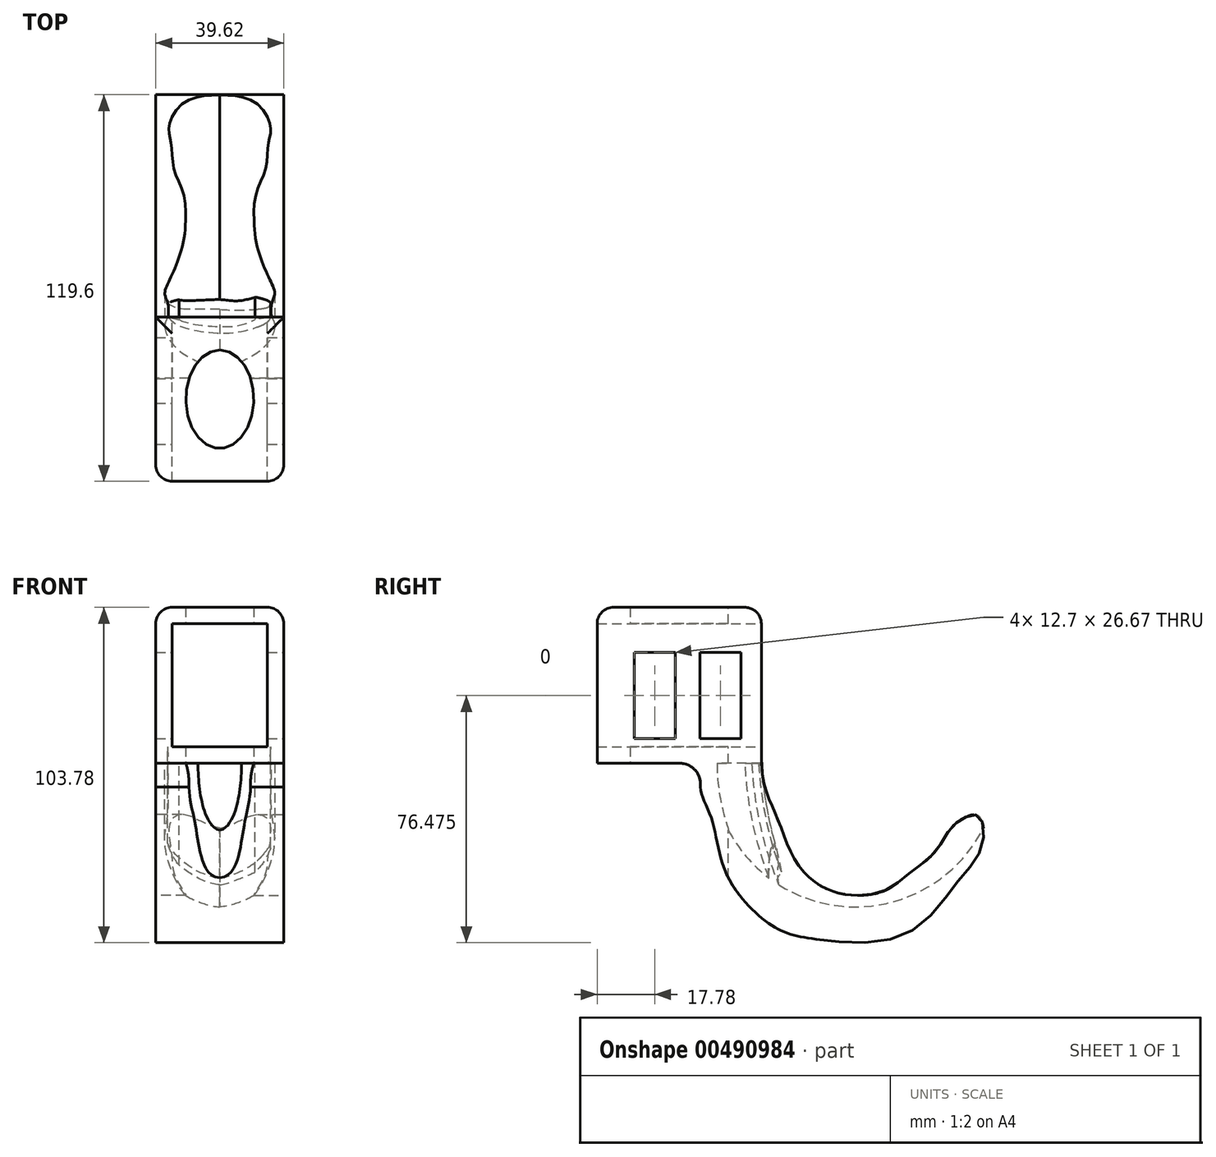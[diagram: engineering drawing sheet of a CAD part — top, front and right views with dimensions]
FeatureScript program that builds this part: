
annotation { "Feature Type Name" : "Feature", "Feature Type Description" : "" }
export const myFeature = defineFeature(function(context is Context, id is Id, definition is map)
    precondition{}
    {
        {
            var Q0;
            Q0=qCreatedBy(makeId("Front.planeOp"),FACE);
            var sketch = newSketch(context, id + "F0", { "sketchPlane" : qUnion([Q0])});
            skLineSegment(sketch, "E0", {"start": v(0, 0) * mm, "end": v(19.81, 0) * mm});
            skLineSegment(sketch, "E1", {"start": v(19.81, 0) * mm, "end": v(19.81, 48.26) * mm});
            skLineSegment(sketch, "E2", {"start": v(19.81, 48.26) * mm, "end": v(0, 48.26) * mm});
            skLineSegment(sketch, "E3.MirrorCS", {"start": v(0, 0) * mm, "end": v(-19.81, 0) * mm});
            skLineSegment(sketch, "E4.MirrorCS", {"start": v(-19.81, 0) * mm, "end": v(-19.81, 48.26) * mm});
            skLineSegment(sketch, "E5.MirrorCS", {"start": v(-19.81, 48.26) * mm, "end": v(0, 48.26) * mm});
            skLineSegment(sketch, "E6.0", {"start": v(-14.73, 5.08) * mm, "end": v(-14.73, 43.18) * mm});
            skLineSegment(sketch, "E6.1", {"start": v(14.73, 43.18) * mm, "end": v(0, 43.18) * mm});
            skLineSegment(sketch, "E6.2", {"start": v(14.73, 5.08) * mm, "end": v(14.73, 43.18) * mm});
            skLineSegment(sketch, "E6.3", {"start": v(-14.73, 43.18) * mm, "end": v(0, 43.18) * mm});
            skLineSegment(sketch, "E6.4", {"start": v(0, 5.08) * mm, "end": v(14.73, 5.08) * mm});
            skLineSegment(sketch, "E6.5", {"start": v(0, 5.08) * mm, "end": v(-14.73, 5.08) * mm});
            skSolve(sketch);
        }
        {
            var Q0;
            Q0 = qSketchRegion(id + "F0", true);
            extrude(context, id + "F1", {"entities" : qUnion([Q0]), "depth" : 50.8 * mm});
        }
        {
            var Q0;
            Q0=qCreatedBy(makeId("Right.planeOp"),FACE);
            var sketch = newSketch(context, id + "F2", { "sketchPlane" : qUnion([Q0])});
            skLineSegment(sketch, "E7.0", {"start": v(-50.8, 0) * mm, "end": v(-25.2, 0) * mm});
            skLineSegment(sketch, "E8", {"start": v(0, 0) * mm, "end": v(0, -1.58) * mm});
            skLineSegment(sketch, "E9", {"start": v(0, -1.58) * mm, "end": v(0, -40.64) * mm, "construction": true});
            skFitSpline(sketch, "E10", {"points": [v(0, 0) * mm, v(4.67, -16.3) * mm, v(11.2, -31.15) * mm, v(20.7, -39.07) * mm, v(29.8, -40.85) * mm, v(38.91, -39.07) * mm, v(46.44, -33.53) * mm, v(53.56, -27.6) * mm, v(58.7, -20.07) * mm, v(63.67, -16.45) * mm, v(67.42, -16.45) * mm, v(68.21, -25.8) * mm, v(60.67, -36.73) * mm, v(44.36, -53) * mm, v(16.9, -54.44) * mm, v(3.5, -50.33) * mm, v(-10.79, -34.25) * mm, v(-15.43, -17.04) * mm, v(-18.85, -7.4) * mm], "startDerivative": vector(15.82, -363.71) * mm, "endDerivative": vector(3.67, 160.8) * mm});
            skLineSegment(sketch, "E11", {"start": v(-18.85, -7.4) * mm, "end": v(-18.85, -6.35) * mm});
            skPoint(sketch, "E12.newPointA", {"position": v(-18.85, 0) * mm});
            skArc(sketch, "E12.filletArc", {"start": v(-18.85, -6.35) * mm, "mid": v(-20.71, -1.86) * mm, "end": v(-25.2, 0) * mm});
            skLineSegment(sketch, "E13", {"start": v(-25.2, 0) * mm, "end": v(0, 0) * mm});
            skLineSegment(sketch, "E14", {"start": v(16.9, -54.44) * mm, "end": v(-63.55, -54.44) * mm});
            skLineSegment(sketch, "E15", {"start": v(29.8, -40.85) * mm, "end": v(-33.2, -40.85) * mm});
            skSolve(sketch);
        }
        {
            var Q0;
            Q0 = qSketchRegion(id + "F2", true);
            var Q1;
            Q1=makeQuery(id+"F1.opExtrude","SWEPT_FACE",FACE,{"disambiguationData":[OSD([sQuery(id+"F0.wireOp",EDGE,"E1")])]});
            var Q2;
            Q2=makeQuery(id+"F1.opExtrude","SWEPT_FACE",FACE,{"disambiguationData":[OSD([sQuery(id+"F0.wireOp",EDGE,"E4.MirrorCS")])]});
            extrude(context, id + "F3", {"entities" : qUnion([Q0]), "operationType" : NewBodyOperationType.ADD, "endBound" : BoundingType.UP_TO_SURFACE, "endBoundEntityFace" : qUnion([Q1]), "depth" : 25.4 * mm, "hasSecondDirection" : true, "secondDirectionBound" : SecondDirectionBoundingType.UP_TO_SURFACE, "secondDirectionOppositeDirection" : true, "secondDirectionBoundEntityFace" : qUnion([Q2]), "secondDirectionDepth" : 25.4 * mm});
        }
        {
            var Q0;
            Q0=qCreatedBy(makeId("Top.planeOp"),FACE);
            var sketch = newSketch(context, id + "F4", { "sketchPlane" : qUnion([Q0])});
            skLineSegment(sketch, "E16", {"start": v(0, 0) * mm, "end": v(14.97, 0) * mm});
            skLineSegment(sketch, "E17", {"start": v(0, -15.33) * mm, "end": v(0, 0) * mm, "construction": true});
            skLineSegment(sketch, "E18", {"start": v(0, 0) * mm, "end": v(0, 3.31) * mm, "construction": true});
            skLineSegment(sketch, "E19", {"start": v(0, 3.31) * mm, "end": v(-16.99, 3.31) * mm});
            skFitSpline(sketch, "E20", {"points": [v(-16.99, 3.31) * mm, v(-14.99, 3) * mm, v(-15.12, 1.3) * mm, v(-16.99, -2.44) * mm, v(-12.29, -10.59) * mm, v(0, -15.33) * mm], "startDerivative": vector(-8.13, -1.44) * mm, "endDerivative": vector(29.7, -1.2) * mm});
            skFitSpline(sketch, "E21.MirrorCS", {"points": [v(16.99, 3.31) * mm, v(14.99, 3) * mm, v(15.12, 1.3) * mm, v(16.99, -2.44) * mm, v(12.29, -10.59) * mm, v(0, -15.33) * mm], "startDerivative": vector(8.13, -1.44) * mm, "endDerivative": vector(-29.7, -1.2) * mm});
            skLineSegment(sketch, "E22.MirrorCS", {"start": v(0, 3.31) * mm, "end": v(16.99, 3.31) * mm});
            skLineSegment(sketch, "E23", {"start": v(-23.44, 29.08) * mm, "end": v(29.75, 29.08) * mm, "construction": true});
            skSolve(sketch);
        }
        {
            var Q0;
            Q0=makeQuery(id+"F4.imprint","IMPRINT",FACE,{"disambiguationData":[TD([[makeQuery(id+"F4.imprint","IMPRINT",EDGE,{"derivedFrom":sQuery(id+"F4.wireOp",EDGE,"E19")}),1.0]])]});
            var Q1;
            Q1=sQuery(id+"F4.wireOp",EDGE,"bd3d4c37-0d49-42ea-b119-917c5ecf52030.MirrorCS");
            var Q2;
            Q2=sQuery(id+"F4.wireOp",EDGE,"e48450e5-2de9-4554-b7ab-408c190373c4");
            var Q3;
            Q3=sQuery(id+"F4.wireOp",EDGE,"aUtNrbl3-2mMZ-NAFI-EfRR-eX0SopnJXztB");
            var Q4;
            Q4=sQuery(id+"F4.wireOp",EDGE,"E23");
            revolve(context, id + "F5", {"operationType" : NewBodyOperationType.REMOVE, "entities" : qUnion([Q0]), "surfaceEntities" : qUnion([Q1, Q2, Q3]), "axis" : qUnion([Q4]), "revolveType" : RevolveType.ONE_DIRECTION, "angle" : 165 * degree});
        }
        {
            var Q0;
            Q0=makeQuery(id+"F1.opExtrude","SWEPT_EDGE",EDGE,{"disambiguationData":[OSD([sQuery(id+"F0.wireOp",EDGE,"E4.MirrorCS"),sQuery(id+"F0.wireOp",EDGE,"E5.MirrorCS")])]});
            var Q1;
            Q1=makeQuery(id+"F1.opExtrude","SWEPT_EDGE",EDGE,{"disambiguationData":[OSD([sQuery(id+"F0.wireOp",EDGE,"E1"),sQuery(id+"F0.wireOp",EDGE,"E2")])]});
            var Q2;
            Q2=makeQuery(id+"F1.opExtrude","CAP_EDGE",EDGE,{"disambiguationData":[OSD([sQuery(id+"F0.wireOp",EDGE,"E4.MirrorCS")])],"isStart":false});
            var Q3;
            Q3=makeQuery(id+"F1.opExtrude","CAP_EDGE",EDGE,{"disambiguationData":[OSD([sQuery(id+"F0.wireOp",EDGE,"E1")])],"isStart":false});
            var Q4;
            Q4=makeQuery(id+"F1.opExtrude","CAP_EDGE",EDGE,{"disambiguationData":[OSD([sQuery(id+"F0.wireOp",EDGE,"E2"),sQuery(id+"F0.wireOp",EDGE,"E5.MirrorCS")])],"isStart":false});
            var Q5;
            Q5=makeQuery(id+"F1.opExtrude","CAP_EDGE",EDGE,{"disambiguationData":[OSD([sQuery(id+"F0.wireOp",EDGE,"E2"),sQuery(id+"F0.wireOp",EDGE,"E5.MirrorCS")])],"isStart":true});
            fillet(context, id + "F6", {"entities" : qUnion([Q0, Q1, Q2, Q3, Q4, Q5]), "radius" : 5.08 * mm, "tangentPropagation" : true, "allowEdgeOverflow" : false});
        }
        {
            var Q0;
            {var subQ0=sQuery(id+"F0.wireOp",EDGE,"E1");Q0=makeQuery(id+"F3.boolean.opBoolean","MERGE",FACE,{"derivedFrom":[makeQuery(id+"F1.opExtrude","SWEPT_FACE",FACE,{"disambiguationData":[OSD([subQ0])]}),makeQuery(id+"F3.opExtrude","CAP_FACE",FACE,{"disambiguationData":[OSD([subQ0])],"isStart":false})]});}
            var sketch = newSketch(context, id + "F7", { "sketchPlane" : qUnion([Q0])});
            skLineSegment(sketch, "E24.0", {"start": v(-45.72, 43.18) * mm, "end": v(-45.72, 0) * mm});
            skLineSegment(sketch, "E25", {"start": v(-33.02, 43.18) * mm, "end": v(-33.02, 0) * mm, "construction": true});
            skLineSegment(sketch, "E26", {"start": v(-12.7, 43.18) * mm, "end": v(-12.7, 0) * mm, "construction": true});
            skPoint(sketch, "E27.3.internal.snap0", {"position": v(-33.02, 21.59) * mm});
            skLineSegment(sketch, "E28", {"start": v(-22.86, 34.3) * mm, "end": v(-22.86, 7.62) * mm, "construction": true});
            skLineSegment(sketch, "E29", {"start": v(0, 0) * mm, "end": v(0, 43.18) * mm});
            skLineSegment(sketch, "E30", {"start": v(-33.02, 34.3) * mm, "end": v(-39.37, 34.3) * mm});
            skLineSegment(sketch, "E31", {"start": v(-39.37, 34.3) * mm, "end": v(-39.37, 7.62) * mm});
            skLineSegment(sketch, "E32", {"start": v(-39.37, 7.62) * mm, "end": v(-33.02, 7.62) * mm});
            skLineSegment(sketch, "E33.MirrorCS", {"start": v(-26.67, 34.3) * mm, "end": v(-26.67, 7.62) * mm});
            skLineSegment(sketch, "E34.MirrorCS", {"start": v(-19.05, 34.3) * mm, "end": v(-19.05, 7.62) * mm});
            skLineSegment(sketch, "E35.MirrorCS", {"start": v(-6.35, 34.3) * mm, "end": v(-6.35, 7.62) * mm});
            skLineSegment(sketch, "E36.MirrorCS", {"start": v(-26.67, 7.62) * mm, "end": v(-33.02, 7.62) * mm});
            skLineSegment(sketch, "E37.MirrorCS", {"start": v(-33.02, 34.3) * mm, "end": v(-26.67, 34.3) * mm});
            skLineSegment(sketch, "E38.MirrorCS", {"start": v(-12.7, 34.3) * mm, "end": v(-19.05, 34.3) * mm});
            skLineSegment(sketch, "E39.MirrorCS", {"start": v(-19.05, 7.62) * mm, "end": v(-12.7, 7.62) * mm});
            skLineSegment(sketch, "E40.MirrorCS", {"start": v(-12.7, 34.3) * mm, "end": v(-6.35, 34.3) * mm});
            skLineSegment(sketch, "E41.MirrorCS", {"start": v(-6.35, 7.62) * mm, "end": v(-12.7, 7.62) * mm});
            skSolve(sketch);
        }
        {
            var Q0;
            Q0 = qSketchRegion(id + "F7", true);
            extrude(context, id + "F8", {"entities" : qUnion([Q0]), "operationType" : NewBodyOperationType.REMOVE, "endBound" : BoundingType.THROUGH_ALL, "oppositeDirection" : true, "depth" : 25.4 * mm});
        }
        {
            var Q0;
            Q0=makeQuery(id+"F1.opExtrude","SWEPT_FACE",FACE,{"disambiguationData":[OSD([sQuery(id+"F0.wireOp",EDGE,"E6.4"),sQuery(id+"F0.wireOp",EDGE,"E6.5")])]});
            var sketch = newSketch(context, id + "F9", { "sketchPlane" : qUnion([Q0])});
            skFitSpline(sketch, "E42", {"points": [v(-16.14, 0) * mm, v(-13.37, -2.36) * mm, v(-9.02, -3.9) * mm, v(0, -5.08) * mm, v(8.2, -4.2) * mm, v(13.64, -2.32) * mm, v(15.68, 0) * mm], "startDerivative": vector(17.41, -19.76) * mm, "endDerivative": vector(0.43, 26.38) * mm});
            skFitSpline(sketch, "E43", {"points": [v(13.64, -2.32) * mm, v(11.6, -3.2) * mm], "startDerivative": vector(-1.77, -0.76) * mm, "endDerivative": vector(-1.77, -0.76) * mm});
            skLineSegment(sketch, "E44", {"start": v(-16.14, 0) * mm, "end": v(-12.65, -0.9) * mm});
            skLineSegment(sketch, "E45", {"start": v(15.68, 0) * mm, "end": v(10.9, -0.9) * mm});
            skFitSpline(sketch, "E46", {"points": [v(-12.65, -0.9) * mm, v(-10.12, -1.84) * mm, v(-3.58, -2.84) * mm, v(0, -3.02) * mm, v(5.55, -2.78) * mm, v(10.9, -0.9) * mm], "startDerivative": vector(13.83, -6.5) * mm, "endDerivative": vector(23.5, 10.5) * mm});
            skLineSegment(sketch, "E47", {"start": v(-20.97, 108.82) * mm, "end": v(27.1, 108.82) * mm, "construction": true});
            skSolve(sketch);
        }
        {
            var Q0;
            Q0 = qSketchRegion(id + "F9", true);
            var Q1;
            Q1=sQuery(id+"F9.wireOp",EDGE,"E47");
            revolve(context, id + "F10", {"operationType" : NewBodyOperationType.ADD, "entities" : qUnion([Q0]), "axis" : qUnion([Q1]), "revolveType" : RevolveType.ONE_DIRECTION, "angle" : 25 * degree});
        }
        {
            var Q0;
            Q0=makeQuery(id+"F1.opExtrude","SWEPT_FACE",FACE,{"disambiguationData":[OSD([sQuery(id+"F0.wireOp",EDGE,"E2"),sQuery(id+"F0.wireOp",EDGE,"E5.MirrorCS")])]});
            var sketch = newSketch(context, id + "F11", { "sketchPlane" : qUnion([Q0])});
            skEllipse(sketch, "E48", {"center": v(0, -25.4) * mm, "majorRadius": 15.2 * mm, "minorRadius": 10.52 * mm, "majorAxis": v(0, 1)});
            skPoint(sketch, "E48.centerSnap0", {"position": v(14.73, -25.4) * mm});
            skPoint(sketch, "E48.centerSnap1", {"position": v(0, -5.08) * mm});
            skSolve(sketch);
        }
        {
            var Q0;
            Q0 = qSketchRegion(id + "F11", true);
            extrude(context, id + "F12", {"entities" : qUnion([Q0]), "operationType" : NewBodyOperationType.REMOVE, "oppositeDirection" : true, "depth" : 117.4 * mm});
        }
    });
